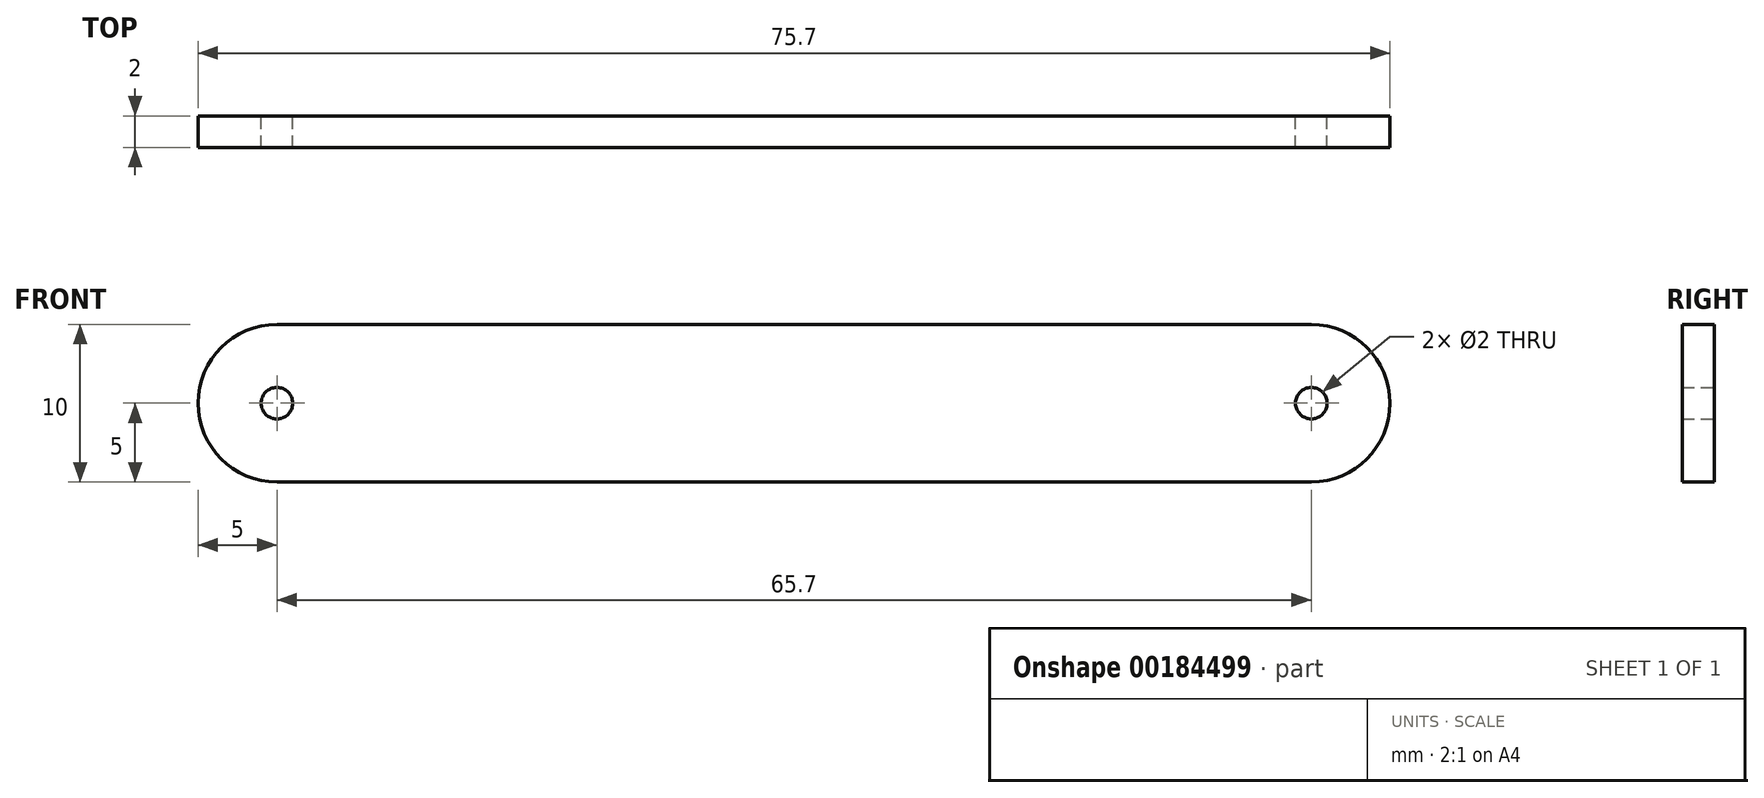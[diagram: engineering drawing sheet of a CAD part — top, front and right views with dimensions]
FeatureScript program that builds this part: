
annotation { "Feature Type Name" : "Feature", "Feature Type Description" : "" }
export const myFeature = defineFeature(function(context is Context, id is Id, definition is map)
    precondition{}
    {
        {
            var Q0;
            Q0=qCreatedBy(makeId("Front.planeOp"),FACE);
            var sketch = newSketch(context, id + "F0", { "sketchPlane" : qUnion([Q0])});
            skLineSegment(sketch, "E0.bottom", {"start": v(0, 0) * mm, "end": v(75.7, 0) * mm});
            skLineSegment(sketch, "E0.top", {"start": v(0, -10) * mm, "end": v(75.7, -10) * mm});
            skLineSegment(sketch, "E0.left", {"start": v(0, 0) * mm, "end": v(0, -10) * mm});
            skLineSegment(sketch, "E0.right", {"start": v(75.7, 0) * mm, "end": v(75.7, -10) * mm});
            skCircle(sketch, "E1", {"center": v(5, -5) * mm, "radius": 1 * mm});
            skPoint(sketch, "E1.centerSnap0", {"position": v(0, -5) * mm});
            skCircle(sketch, "E2", {"center": v(70.7, -5) * mm, "radius": 1 * mm});
            skSolve(sketch);
        }
        {
            var Q0;
            Q0 = qSketchRegion(id + "F0", true);
            extrude(context, id + "F1", {"entities" : qUnion([Q0]), "depth" : 2 * mm});
        }
        {
            var Q0;
            Q0=makeQuery(id+"F1.opExtrude","SWEPT_EDGE",EDGE,{"disambiguationData":[OSD([sQuery(id+"F0.wireOp",EDGE,"E0.bottom"),sQuery(id+"F0.wireOp",EDGE,"E0.left")])]});
            fillet(context, id + "F2", {"entities" : qUnion([Q0]), "radius" : 5 * mm, "tangentPropagation" : true, "allowEdgeOverflow" : false});
        }
        {
            var Q0;
            Q0=makeQuery(id+"F1.opExtrude","SWEPT_EDGE",EDGE,{"disambiguationData":[OSD([sQuery(id+"F0.wireOp",EDGE,"E0.top"),sQuery(id+"F0.wireOp",EDGE,"E0.left")])]});
            fillet(context, id + "F3", {"entities" : qUnion([Q0]), "radius" : 5 * mm, "tangentPropagation" : true, "allowEdgeOverflow" : false});
        }
        {
            var Q0;
            Q0=makeQuery(id+"F1.opExtrude","SWEPT_EDGE",EDGE,{"disambiguationData":[OSD([sQuery(id+"F0.wireOp",EDGE,"E0.top"),sQuery(id+"F0.wireOp",EDGE,"E0.right")])]});
            fillet(context, id + "F4", {"entities" : qUnion([Q0]), "radius" : 5 * mm, "tangentPropagation" : true, "allowEdgeOverflow" : false});
        }
        {
            var Q0;
            Q0=makeQuery(id+"F1.opExtrude","SWEPT_EDGE",EDGE,{"disambiguationData":[OSD([sQuery(id+"F0.wireOp",EDGE,"E0.bottom"),sQuery(id+"F0.wireOp",EDGE,"E0.right")])]});
            fillet(context, id + "F5", {"entities" : qUnion([Q0]), "radius" : 5 * mm, "tangentPropagation" : true, "allowEdgeOverflow" : false});
        }
    });
